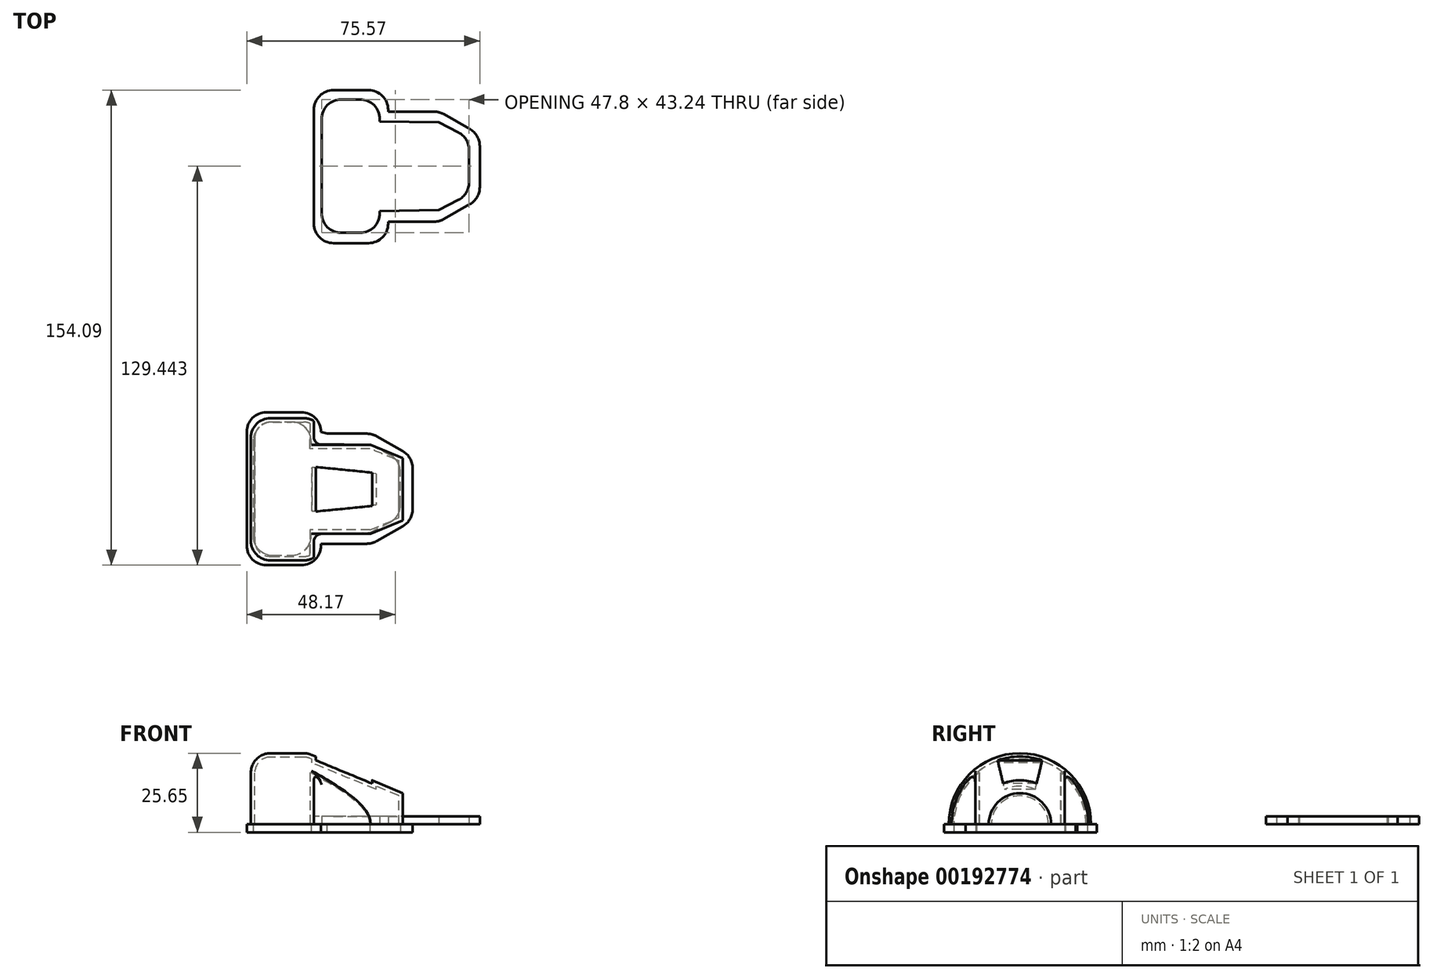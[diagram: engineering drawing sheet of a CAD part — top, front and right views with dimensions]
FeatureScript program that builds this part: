
annotation { "Feature Type Name" : "Feature", "Feature Type Description" : "" }
export const myFeature = defineFeature(function(context is Context, id is Id, definition is map)
    precondition{}
    {
        {
            var Q0;
            Q0=qCreatedBy(makeId("Top.planeOp"),FACE);
            var sketch = newSketch(context, id + "F0", { "sketchPlane" : qUnion([Q0])});
            skLineSegment(sketch, "E0.right", {"start": v(46.79, -59.1) * mm, "end": v(46.79, -37.32) * mm});
            skLineSegment(sketch, "E1", {"start": v(46.79, -37.32) * mm, "end": v(76.56, -49.84) * mm});
            skLineSegment(sketch, "E2", {"start": v(76.56, -49.84) * mm, "end": v(76.56, -59.1) * mm});
            skLineSegment(sketch, "E3", {"start": v(76.56, -59.1) * mm, "end": v(46.79, -59.1) * mm});
            skLineSegment(sketch, "E4.bottom", {"start": v(29.86, -59.1) * mm, "end": v(46.79, -59.1) * mm});
            skLineSegment(sketch, "E4.top", {"start": v(29.86, -37.32) * mm, "end": v(46.79, -37.32) * mm});
            skLineSegment(sketch, "E4.left", {"start": v(29.86, -59.1) * mm, "end": v(29.86, -37.32) * mm});
            skSolve(sketch);
        }
        {
            var Q0;
            Q0=qCreatedBy(makeId("Top.planeOp"),FACE);
            var sketch = newSketch(context, id + "F1", { "sketchPlane" : qUnion([Q0])});
            skLineSegment(sketch, "E5", {"start": v(49.04, 32.89) * mm, "end": v(49.04, 27.09) * mm});
            skLineSegment(sketch, "E6", {"start": v(55.39, 20.74) * mm, "end": v(66.76, 20.74) * mm});
            skLineSegment(sketch, "E7", {"start": v(73.1, 27.09) * mm, "end": v(73.1, 27.7) * mm});
            skLineSegment(sketch, "E8", {"start": v(73.1, 27.7) * mm, "end": v(88, 27.7) * mm});
            skLineSegment(sketch, "E9", {"start": v(-9.46, 33.17) * mm, "end": v(-27.89, 38.87) * mm});
            skLineSegment(sketch, "E10", {"start": v(91.13, 28.53) * mm, "end": v(99.61, 33.36) * mm});
            skLineSegment(sketch, "E11", {"start": v(102.82, 38.88) * mm, "end": v(102.82, 45.55) * mm});
            skLineSegment(sketch, "E12", {"start": v(-32.36, 44.94) * mm, "end": v(-32.36, 45.55) * mm});
            skLineSegment(sketch, "E13.MirrorCS", {"start": v(-32.36, 46.16) * mm, "end": v(-32.36, 45.55) * mm});
            skLineSegment(sketch, "E14.MirrorCS", {"start": v(-9.46, 57.93) * mm, "end": v(-27.89, 52.23) * mm});
            skLineSegment(sketch, "E15.MirrorCS", {"start": v(49.04, 58.2) * mm, "end": v(49.04, 64) * mm});
            skLineSegment(sketch, "E16.MirrorCS", {"start": v(55.39, 70.36) * mm, "end": v(66.76, 70.36) * mm});
            skLineSegment(sketch, "E17.MirrorCS", {"start": v(73.1, 64) * mm, "end": v(73.1, 63.4) * mm});
            skLineSegment(sketch, "E18.MirrorCS", {"start": v(73.1, 63.4) * mm, "end": v(88, 63.4) * mm});
            skLineSegment(sketch, "E19.MirrorCS", {"start": v(91.13, 62.56) * mm, "end": v(99.61, 57.74) * mm});
            skLineSegment(sketch, "E20.MirrorCS", {"start": v(102.82, 52.22) * mm, "end": v(102.82, 45.55) * mm});
            skPoint(sketch, "E21.visualSharp", {"position": v(49.04, 20.74) * mm});
            skArc(sketch, "E21.filletArc", {"start": v(49.04, 27.09) * mm, "mid": v(50.9, 22.6) * mm, "end": v(55.39, 20.74) * mm});
            skPoint(sketch, "E22.visualSharp", {"position": v(73.1, 20.74) * mm});
            skArc(sketch, "E22.filletArc", {"start": v(66.76, 20.74) * mm, "mid": v(71.25, 22.6) * mm, "end": v(73.1, 27.09) * mm});
            skPoint(sketch, "E23.visualSharp", {"position": v(49.04, 70.36) * mm});
            skArc(sketch, "E23.filletArc", {"start": v(55.39, 70.36) * mm, "mid": v(50.9, 68.5) * mm, "end": v(49.04, 64) * mm});
            skPoint(sketch, "E24.visualSharp", {"position": v(73.1, 70.36) * mm});
            skArc(sketch, "E24.filletArc", {"start": v(73.1, 64) * mm, "mid": v(71.25, 68.5) * mm, "end": v(66.76, 70.36) * mm});
            skPoint(sketch, "E25.visualSharp", {"position": v(102.82, 55.91) * mm});
            skArc(sketch, "E25.filletArc", {"start": v(102.82, 52.22) * mm, "mid": v(101.96, 55.41) * mm, "end": v(99.61, 57.74) * mm});
            skPoint(sketch, "E26.visualSharp", {"position": v(102.82, 35.18) * mm});
            skArc(sketch, "E26.filletArc", {"start": v(99.61, 33.36) * mm, "mid": v(101.96, 35.68) * mm, "end": v(102.82, 38.88) * mm});
            skPoint(sketch, "E27.visualSharp", {"position": v(89.67, 63.4) * mm});
            skArc(sketch, "E27.filletArc", {"start": v(91.13, 62.56) * mm, "mid": v(89.62, 63.18) * mm, "end": v(88, 63.4) * mm});
            skPoint(sketch, "E28.visualSharp", {"position": v(89.67, 27.7) * mm});
            skArc(sketch, "E28.filletArc", {"start": v(88, 27.7) * mm, "mid": v(89.62, 27.91) * mm, "end": v(91.13, 28.53) * mm});
            skPoint(sketch, "E29.visualSharp", {"position": v(-8.54, 58.2) * mm});
            skArc(sketch, "E29.filletArc", {"start": v(-7.58, 58.2) * mm, "mid": v(-8.53, 58.14) * mm, "end": v(-9.46, 57.93) * mm});
            skPoint(sketch, "E30.visualSharp", {"position": v(-8.54, 32.89) * mm});
            skArc(sketch, "E30.filletArc", {"start": v(-9.46, 33.17) * mm, "mid": v(-8.53, 32.96) * mm, "end": v(-7.58, 32.89) * mm});
            skPoint(sketch, "E31.visualSharp", {"position": v(-32.36, 40.25) * mm});
            skArc(sketch, "E31.filletArc", {"start": v(-32.36, 44.94) * mm, "mid": v(-31.12, 41.17) * mm, "end": v(-27.89, 38.87) * mm});
            skPoint(sketch, "E32.visualSharp", {"position": v(-32.36, 50.84) * mm});
            skArc(sketch, "E32.filletArc", {"start": v(-27.89, 52.23) * mm, "mid": v(-31.12, 49.93) * mm, "end": v(-32.36, 46.16) * mm});
            skLineSegment(sketch, "E33", {"start": v(49.04, 58.2) * mm, "end": v(49.04, 32.89) * mm});
            skSolve(sketch);
        }
        {
            var Q0;
            Q0=makeQuery(id+"F0.imprint","IMPRINT",FACE,{"disambiguationData":[TD([[makeQuery(id+"F0.imprint","IMPRINT",EDGE,{"derivedFrom":sQuery(id+"F0.wireOp",EDGE,"E4.bottom")}),1.0]])]});
            var Q1;
            Q1=makeQuery(id+"F0.imprint","IMPRINT",FACE,{"disambiguationData":[TD([[makeQuery(id+"F0.imprint","IMPRINT",EDGE,{"derivedFrom":sQuery(id+"F0.wireOp",EDGE,"E1")}),-1.0]])]});
            var Q2;
            Q2=sQuery(id+"F0.wireOp",EDGE,"E4.bottom");
            revolve(context, id + "F2", {"entities" : qUnion([Q0, Q1]), "axis" : qUnion([Q2]), "revolveType" : RevolveType.ONE_DIRECTION, "angle" : 180 * degree});
        }
        {
            var Q0;
            Q0=makeQuery(id+"F2.opRevolve","SWEPT_EDGE",EDGE,{"disambiguationData":[OSD([sQuery(id+"F0.wireOp",EDGE,"E1"),sQuery(id+"F0.wireOp",EDGE,"E4.top"),sQuery(id+"F0.wireOp",EDGE,"E0.right")])]});
            var Q1;
            Q1=makeQuery(id+"F2.opRevolve","SWEPT_EDGE",EDGE,{"disambiguationData":[OSD([sQuery(id+"F0.wireOp",EDGE,"E4.top"),sQuery(id+"F0.wireOp",EDGE,"E4.left")])]});
            fillet(context, id + "F3", {"entities" : qUnion([Q0, Q1]), "radius" : 5.08 * mm, "tangentPropagation" : true, "allowEdgeOverflow" : false});
        }
        {
            var Q0;
            Q0=qCreatedBy(makeId("Top.planeOp"),FACE);
            var sketch = newSketch(context, id + "F4", { "sketchPlane" : qUnion([Q0])});
            skLineSegment(sketch, "E34.0.0", {"start": v(34.94, -37.32) * mm, "end": v(45.76, -37.32) * mm});
            skArc(sketch, "E34.0.1", {"start": v(45.76, -37.32) * mm, "mid": v(46.77, -37.42) * mm, "end": v(47.73, -37.71) * mm});
            skLineSegment(sketch, "E34.0.2", {"start": v(47.73, -37.71) * mm, "end": v(76.56, -49.84) * mm});
            skLineSegment(sketch, "E34.0.3", {"start": v(76.56, -49.84) * mm, "end": v(76.56, -68.37) * mm});
            skLineSegment(sketch, "E34.0.4", {"start": v(76.56, -68.37) * mm, "end": v(47.73, -80.5) * mm});
            skArc(sketch, "E34.0.5", {"start": v(47.73, -80.5) * mm, "mid": v(46.77, -80.8) * mm, "end": v(45.76, -80.9) * mm});
            skLineSegment(sketch, "E34.0.6", {"start": v(45.76, -80.9) * mm, "end": v(34.94, -80.9) * mm});
            skArc(sketch, "E34.0.7", {"start": v(34.94, -80.9) * mm, "mid": v(31.35, -79.4) * mm, "end": v(29.86, -75.82) * mm});
            skLineSegment(sketch, "E34.0.8", {"start": v(29.86, -75.82) * mm, "end": v(29.86, -42.4) * mm});
            skArc(sketch, "E34.0.9", {"start": v(29.86, -42.4) * mm, "mid": v(31.35, -38.8) * mm, "end": v(34.94, -37.32) * mm});
            skLineSegment(sketch, "E35", {"start": v(47.73, -82.32) * mm, "end": v(47.73, -72.3) * mm});
            skLineSegment(sketch, "E36", {"start": v(47.73, -72.3) * mm, "end": v(75.84, -72.3) * mm});
            skLineSegment(sketch, "E37", {"start": v(75.84, -72.3) * mm, "end": v(75.51, -83.4) * mm});
            skLineSegment(sketch, "E38", {"start": v(75.51, -83.4) * mm, "end": v(47.73, -82.32) * mm});
            skLineSegment(sketch, "E39.MirrorCS", {"start": v(47.73, -45.9) * mm, "end": v(75.84, -45.9) * mm});
            skLineSegment(sketch, "E40.MirrorCS", {"start": v(75.51, -34.8) * mm, "end": v(47.73, -35.89) * mm});
            skLineSegment(sketch, "E41.MirrorCS", {"start": v(47.73, -35.89) * mm, "end": v(47.73, -45.9) * mm});
            skLineSegment(sketch, "E42.MirrorCS", {"start": v(75.84, -45.9) * mm, "end": v(75.51, -34.8) * mm});
            skSolve(sketch);
        }
        {
            var Q0;
            {var subQ0=sQuery(id+"F4.wireOp",EDGE,"E35");var subQ3=sQuery(id+"F4.wireOp",EDGE,"E36");var subQ5=makeQuery(id+"F4.imprint","INTERSECT",VERTEX,{"derivedFrom":[subQ0,subQ3]});Q0=makeQuery(id+"F4.imprint","IMPRINT",FACE,{"disambiguationData":[TD([[makeQuery(id+"F4.imprint","IMPRINT",EDGE,{"disambiguationData":[TD([[subQ5,-1.0]])],"derivedFrom":subQ3}),-1.0]])]});}
            var Q1;
            {var subQ0=sQuery(id+"F4.wireOp",EDGE,"E41.MirrorCS");var subQ3=sQuery(id+"F4.wireOp",EDGE,"E39.MirrorCS");var subQ5=makeQuery(id+"F4.imprint","INTERSECT",VERTEX,{"derivedFrom":[subQ3,subQ0]});Q1=makeQuery(id+"F4.imprint","IMPRINT",FACE,{"disambiguationData":[TD([[makeQuery(id+"F4.imprint","IMPRINT",EDGE,{"disambiguationData":[TD([[subQ5,-1.0]])],"derivedFrom":subQ3}),1.0]])]});}
            var Q2;
            {var subQ3=sQuery(id+"F4.wireOp",EDGE,"E40.MirrorCS");Q2=makeQuery(id+"F4.imprint","IMPRINT",FACE,{"disambiguationData":[TD([[makeQuery(id+"F4.imprint","IMPRINT",EDGE,{"derivedFrom":subQ3}),1.0]])]});}
            var Q3;
            {var subQ0=sQuery(id+"F4.wireOp",EDGE,"E37");Q3=makeQuery(id+"F4.imprint","IMPRINT",FACE,{"disambiguationData":[TD([[makeQuery(id+"F4.imprint","IMPRINT",EDGE,{"derivedFrom":subQ0}),-1.0]])]});}
            extrude(context, id + "F5", {"entities" : qUnion([Q0, Q1, Q2, Q3]), "operationType" : NewBodyOperationType.REMOVE, "depth" : 25.4 * mm});
        }
        {
            var Q0;
            Q0=makeQuery(id+"F5.boolean.opBoolean","COPY",FACE,{"derivedFrom":makeQuery(id+"F5.opExtrude","SWEPT_FACE",FACE,{"disambiguationData":[OSD([sQuery(id+"F4.wireOp",EDGE,"E36")])]})});
            var sketch = newSketch(context, id + "F6", { "sketchPlane" : qUnion([Q0])});
            skLineSegment(sketch, "E43", {"start": v(48.34, 28.45) * mm, "end": v(48.34, 19.91) * mm});
            skLineSegment(sketch, "E44", {"start": v(48.34, 19.91) * mm, "end": v(69.19, 11.32) * mm});
            skLineSegment(sketch, "E45", {"start": v(69.19, 11.32) * mm, "end": v(69.19, 27.77) * mm});
            skLineSegment(sketch, "E46", {"start": v(69.19, 27.77) * mm, "end": v(48.34, 28.45) * mm});
            skSolve(sketch);
        }
        {
            var Q0;
            Q0=makeQuery(id+"F6.imprint","IMPRINT",FACE,{"disambiguationData":[TD([[makeQuery(id+"F6.imprint","IMPRINT",EDGE,{"derivedFrom":sQuery(id+"F6.wireOp",EDGE,"E43")}),1.0]])]});
            extrude(context, id + "F7", {"entities" : qUnion([Q0]), "operationType" : NewBodyOperationType.REMOVE, "oppositeDirection" : true, "depth" : 50.8 * mm});
        }
        {
            var Q0;
            Q0=makeQuery(id+"F2.opRevolve","CAP_FACE",FACE,{"disambiguationData":[OSD([sQuery(id+"F0.wireOp",EDGE,"E1"),sQuery(id+"F0.wireOp",EDGE,"E2"),sQuery(id+"F0.wireOp",EDGE,"E3"),sQuery(id+"F0.wireOp",EDGE,"E4.bottom"),sQuery(id+"F0.wireOp",EDGE,"E4.top"),sQuery(id+"F0.wireOp",EDGE,"E4.left")])],"isStart":false});
            shell(context, id + "F8", {"entities" : qUnion([Q0]), "thickness" : 1.27 * mm, "oppositeDirection" : true});
        }
        {
            var Q0;
            Q0=makeQuery(id+"F1.imprint","IMPRINT",FACE,{"disambiguationData":[TD([[makeQuery(id+"F1.imprint","IMPRINT",EDGE,{"derivedFrom":sQuery(id+"F1.wireOp",EDGE,"E5")}),1.0]])]});
            extrude(context, id + "F9", {"entities" : qUnion([Q0]), "depth" : 2.54 * mm});
        }
        {
            var Q0;
            Q0=makeQuery(id+"F1.imprint","IMPRINT",FACE,{"disambiguationData":[TD([[makeQuery(id+"F1.imprint","IMPRINT",EDGE,{"derivedFrom":sQuery(id+"F1.wireOp",EDGE,"E5")}),1.0]])]});
            var sketch = newSketch(context, id + "F10", { "sketchPlane" : qUnion([Q0])});
            skLineSegment(sketch, "E47", {"start": v(103.17, 45.71) * mm, "end": v(28.73, 45.71) * mm, "construction": true});
            skLineSegment(sketch, "E48", {"start": v(51.52, 45.71) * mm, "end": v(51.52, 30.44) * mm});
            skLineSegment(sketch, "E49", {"start": v(57.87, 24.1) * mm, "end": v(64.04, 24.1) * mm});
            skLineSegment(sketch, "E50", {"start": v(70.39, 30.44) * mm, "end": v(70.39, 31.17) * mm});
            skLineSegment(sketch, "E51", {"start": v(70.39, 31.17) * mm, "end": v(89.48, 31.46) * mm});
            skLineSegment(sketch, "E52", {"start": v(89.48, 31.46) * mm, "end": v(95.88, 34.76) * mm});
            skLineSegment(sketch, "E53", {"start": v(112.09, -4.68) * mm, "end": v(112.09, -10.48) * mm});
            skLineSegment(sketch, "E54", {"start": v(118.44, -16.83) * mm, "end": v(129.8, -16.83) * mm});
            skLineSegment(sketch, "E55", {"start": v(136.15, -10.48) * mm, "end": v(136.15, -9.86) * mm});
            skLineSegment(sketch, "E56", {"start": v(136.15, -9.86) * mm, "end": v(151.04, -9.86) * mm});
            skLineSegment(sketch, "E57", {"start": v(154.18, -9.03) * mm, "end": v(162.66, -4.2) * mm});
            skLineSegment(sketch, "E58", {"start": v(165.87, 1.31) * mm, "end": v(165.87, 7.99) * mm});
            skLineSegment(sketch, "E59.MirrorCS", {"start": v(112.09, 20.65) * mm, "end": v(112.09, 26.45) * mm});
            skLineSegment(sketch, "E60.MirrorCS", {"start": v(118.44, 32.8) * mm, "end": v(129.8, 32.8) * mm});
            skLineSegment(sketch, "E61.MirrorCS", {"start": v(136.15, 26.45) * mm, "end": v(136.15, 25.83) * mm});
            skLineSegment(sketch, "E62.MirrorCS", {"start": v(136.15, 25.83) * mm, "end": v(151.04, 25.83) * mm});
            skLineSegment(sketch, "E63.MirrorCS", {"start": v(154.18, 25) * mm, "end": v(162.66, 20.18) * mm});
            skLineSegment(sketch, "E64.MirrorCS", {"start": v(165.87, 14.66) * mm, "end": v(165.87, 7.99) * mm});
            skPoint(sketch, "E65.visualSharp", {"position": v(112.09, -16.83) * mm});
            skArc(sketch, "E65.filletArc", {"start": v(112.09, -10.48) * mm, "mid": v(113.95, -14.97) * mm, "end": v(118.44, -16.83) * mm});
            skPoint(sketch, "E66.visualSharp", {"position": v(136.15, -16.83) * mm});
            skArc(sketch, "E66.filletArc", {"start": v(129.8, -16.83) * mm, "mid": v(134.3, -14.97) * mm, "end": v(136.15, -10.48) * mm});
            skPoint(sketch, "E67.visualSharp", {"position": v(112.09, 32.8) * mm});
            skArc(sketch, "E67.filletArc", {"start": v(118.44, 32.8) * mm, "mid": v(113.95, 30.94) * mm, "end": v(112.09, 26.45) * mm});
            skPoint(sketch, "E68.visualSharp", {"position": v(136.15, 32.8) * mm});
            skArc(sketch, "E68.filletArc", {"start": v(136.15, 26.45) * mm, "mid": v(134.3, 30.94) * mm, "end": v(129.8, 32.8) * mm});
            skPoint(sketch, "E69.visualSharp", {"position": v(165.87, 18.35) * mm});
            skArc(sketch, "E69.filletArc", {"start": v(165.87, 14.66) * mm, "mid": v(165, 17.85) * mm, "end": v(162.66, 20.18) * mm});
            skPoint(sketch, "E70.visualSharp", {"position": v(165.87, -2.38) * mm});
            skArc(sketch, "E70.filletArc", {"start": v(162.66, -4.2) * mm, "mid": v(165, -1.88) * mm, "end": v(165.87, 1.31) * mm});
            skPoint(sketch, "E71.visualSharp", {"position": v(152.72, 25.83) * mm});
            skArc(sketch, "E71.filletArc", {"start": v(154.18, 25) * mm, "mid": v(152.66, 25.62) * mm, "end": v(151.04, 25.83) * mm});
            skPoint(sketch, "E72.visualSharp", {"position": v(152.72, -9.86) * mm});
            skArc(sketch, "E72.filletArc", {"start": v(151.04, -9.86) * mm, "mid": v(152.66, -9.65) * mm, "end": v(154.18, -9.03) * mm});
            skLineSegment(sketch, "E73", {"start": v(112.09, 20.65) * mm, "end": v(112.09, -4.68) * mm});
            skLineSegment(sketch, "E74", {"start": v(99.32, 45.71) * mm, "end": v(99.32, 40.4) * mm});
            skLineSegment(sketch, "E75.MirrorCS", {"start": v(99.32, 45.71) * mm, "end": v(99.32, 51.02) * mm});
            skLineSegment(sketch, "E76.MirrorCS", {"start": v(89.48, 59.97) * mm, "end": v(95.88, 56.67) * mm});
            skLineSegment(sketch, "E77.MirrorCS", {"start": v(70.39, 60.98) * mm, "end": v(70.39, 60.26) * mm});
            skLineSegment(sketch, "E78.MirrorCS", {"start": v(70.39, 60.26) * mm, "end": v(89.48, 59.97) * mm});
            skLineSegment(sketch, "E79.MirrorCS", {"start": v(57.87, 67.33) * mm, "end": v(64.04, 67.33) * mm});
            skLineSegment(sketch, "E80.MirrorCS", {"start": v(51.52, 45.71) * mm, "end": v(51.52, 60.98) * mm});
            skPoint(sketch, "E81.visualSharp", {"position": v(70.39, 24.1) * mm});
            skArc(sketch, "E81.filletArc", {"start": v(64.04, 24.1) * mm, "mid": v(68.53, 25.95) * mm, "end": v(70.39, 30.44) * mm});
            skPoint(sketch, "E82.visualSharp", {"position": v(70.39, 67.33) * mm});
            skArc(sketch, "E82.filletArc", {"start": v(70.39, 60.98) * mm, "mid": v(68.53, 65.47) * mm, "end": v(64.04, 67.33) * mm});
            skPoint(sketch, "E83.visualSharp", {"position": v(51.52, 24.1) * mm});
            skArc(sketch, "E83.filletArc", {"start": v(51.52, 30.44) * mm, "mid": v(53.38, 25.95) * mm, "end": v(57.87, 24.1) * mm});
            skPoint(sketch, "E84.newPointB", {"position": v(51.52, 67.33) * mm});
            skArc(sketch, "E84.filletArc", {"start": v(57.87, 67.33) * mm, "mid": v(53.38, 65.47) * mm, "end": v(51.52, 60.98) * mm});
            skPoint(sketch, "E85.visualSharp", {"position": v(99.32, 36.54) * mm});
            skArc(sketch, "E85.filletArc", {"start": v(95.88, 34.76) * mm, "mid": v(98.4, 37.1) * mm, "end": v(99.32, 40.4) * mm});
            skPoint(sketch, "E86.visualSharp", {"position": v(99.32, 54.9) * mm});
            skArc(sketch, "E86.filletArc", {"start": v(99.32, 51.02) * mm, "mid": v(98.4, 54.33) * mm, "end": v(95.88, 56.67) * mm});
            skLineSegment(sketch, "E87", {"start": v(27.25, -72.13) * mm, "end": v(27.25, -77.38) * mm});
            skLineSegment(sketch, "E88", {"start": v(33.6, -83.73) * mm, "end": v(44.97, -83.73) * mm});
            skLineSegment(sketch, "E89", {"start": v(51.32, -77.38) * mm, "end": v(51.32, -76.77) * mm});
            skLineSegment(sketch, "E90", {"start": v(51.32, -76.77) * mm, "end": v(66.2, -76.77) * mm});
            skLineSegment(sketch, "E91", {"start": v(69.34, -75.94) * mm, "end": v(77.82, -71.11) * mm});
            skLineSegment(sketch, "E92", {"start": v(81.03, -65.6) * mm, "end": v(81.03, -59.47) * mm});
            skLineSegment(sketch, "E93.MirrorCS", {"start": v(27.25, -46.8) * mm, "end": v(27.25, -40.46) * mm});
            skLineSegment(sketch, "E94.MirrorCS", {"start": v(33.6, -34.1) * mm, "end": v(44.97, -34.1) * mm});
            skLineSegment(sketch, "E95.MirrorCS", {"start": v(51.32, -40.46) * mm, "end": v(51.32, -41.62) * mm});
            skLineSegment(sketch, "E96.MirrorCS", {"start": v(53.34, -41.07) * mm, "end": v(66.2, -41.07) * mm});
            skLineSegment(sketch, "E97.MirrorCS", {"start": v(69.34, -41.9) * mm, "end": v(77.82, -46.73) * mm});
            skLineSegment(sketch, "E98.MirrorCS", {"start": v(81.03, -52.25) * mm, "end": v(81.03, -59.47) * mm});
            skArc(sketch, "E99.filletArc", {"start": v(27.25, -77.38) * mm, "mid": v(29.1, -81.87) * mm, "end": v(33.6, -83.73) * mm});
            skArc(sketch, "E100.filletArc", {"start": v(44.97, -83.73) * mm, "mid": v(49.46, -81.87) * mm, "end": v(51.32, -77.38) * mm});
            skArc(sketch, "E101.filletArc", {"start": v(33.6, -34.1) * mm, "mid": v(29.1, -35.97) * mm, "end": v(27.25, -40.46) * mm});
            skArc(sketch, "E102.filletArc", {"start": v(51.32, -40.46) * mm, "mid": v(49.46, -35.97) * mm, "end": v(44.97, -34.1) * mm});
            skArc(sketch, "E103.filletArc", {"start": v(81.03, -52.25) * mm, "mid": v(80.17, -49.06) * mm, "end": v(77.82, -46.73) * mm});
            skArc(sketch, "E104.filletArc", {"start": v(77.82, -71.11) * mm, "mid": v(80.17, -68.79) * mm, "end": v(81.03, -65.6) * mm});
            skArc(sketch, "E105.filletArc", {"start": v(69.34, -41.9) * mm, "mid": v(67.82, -41.29) * mm, "end": v(66.2, -41.07) * mm});
            skArc(sketch, "E106.filletArc", {"start": v(66.2, -76.77) * mm, "mid": v(67.82, -76.56) * mm, "end": v(69.34, -75.94) * mm});
            skLineSegment(sketch, "E107", {"start": v(27.25, -46.8) * mm, "end": v(27.25, -72.13) * mm});
            skLineSegment(sketch, "E108", {"start": v(53.34, -41.07) * mm, "end": v(51.32, -40.46) * mm});
            skSolve(sketch);
        }
        {
            var Q0;
            Q0=makeQuery(id+"F10.imprint","IMPRINT",FACE,{"disambiguationData":[TD([[makeQuery(id+"F10.imprint","IMPRINT",EDGE,{"derivedFrom":sQuery(id+"F10.wireOp",EDGE,"E48")}),1.0]])]});
            extrude(context, id + "F11", {"entities" : qUnion([Q0]), "operationType" : NewBodyOperationType.REMOVE, "depth" : 25.4 * mm});
        }
        {
            var Q0;
            Q0=makeQuery(id+"F5.boolean.opBoolean","COPY",EDGE,{"derivedFrom":makeQuery(id+"F5.opExtrude","SWEPT_EDGE",EDGE,{"disambiguationData":[OSD([sQuery(id+"F4.wireOp",EDGE,"E35"),sQuery(id+"F4.wireOp",EDGE,"E36")])]})});
            var Q1;
            Q1=makeQuery(id+"F5.boolean.opBoolean","COPY",EDGE,{"derivedFrom":makeQuery(id+"F5.opExtrude","SWEPT_EDGE",EDGE,{"disambiguationData":[OSD([sQuery(id+"F4.wireOp",EDGE,"E39.MirrorCS"),sQuery(id+"F4.wireOp",EDGE,"E41.MirrorCS")])]})});
            fillet(context, id + "F12", {"entities" : qUnion([Q0, Q1]), "radius" : 2.54 * mm, "tangentPropagation" : true, "allowEdgeOverflow" : false});
        }
        {
            var Q0;
            Q0=makeQuery(id+"F10.imprint","IMPRINT",FACE,{"disambiguationData":[TD([[makeQuery(id+"F10.imprint","IMPRINT",EDGE,{"derivedFrom":sQuery(id+"F10.wireOp",EDGE,"E87")}),1.0]])]});
            extrude(context, id + "F13", {"entities" : qUnion([Q0]), "operationType" : NewBodyOperationType.ADD, "oppositeDirection" : true, "depth" : 2.59 * mm});
        }
        {
            var Q0;
            Q0=makeQuery(id+"F13.opExtrude","CAP_FACE",FACE,{"disambiguationData":[OSD([sQuery(id+"F10.wireOp",EDGE,"E87"),sQuery(id+"F10.wireOp",EDGE,"E88"),sQuery(id+"F10.wireOp",EDGE,"E89"),sQuery(id+"F10.wireOp",EDGE,"E90"),sQuery(id+"F10.wireOp",EDGE,"E91"),sQuery(id+"F10.wireOp",EDGE,"E92"),sQuery(id+"F10.wireOp",EDGE,"E93.MirrorCS"),sQuery(id+"F10.wireOp",EDGE,"E94.MirrorCS"),sQuery(id+"F10.wireOp",EDGE,"E96.MirrorCS"),sQuery(id+"F10.wireOp",EDGE,"E97.MirrorCS"),sQuery(id+"F10.wireOp",EDGE,"E98.MirrorCS"),sQuery(id+"F10.wireOp",EDGE,"E99.filletArc"),sQuery(id+"F10.wireOp",EDGE,"E100.filletArc"),sQuery(id+"F10.wireOp",EDGE,"E104.filletArc"),sQuery(id+"F10.wireOp",EDGE,"E106.filletArc"),sQuery(id+"F10.wireOp",EDGE,"E101.filletArc"),sQuery(id+"F10.wireOp",EDGE,"E102.filletArc"),sQuery(id+"F10.wireOp",EDGE,"E103.filletArc"),sQuery(id+"F10.wireOp",EDGE,"E105.filletArc"),sQuery(id+"F10.wireOp",EDGE,"E107"),sQuery(id+"F10.wireOp",EDGE,"E108")])],"isStart":false});
            var sketch = newSketch(context, id + "F14", { "sketchPlane" : qUnion([Q0])});
            skLineSegment(sketch, "E109", {"start": v(29.28, 59.65) * mm, "end": v(29.28, 43.62) * mm});
            skLineSegment(sketch, "E110", {"start": v(35.63, 37.27) * mm, "end": v(41.8, 37.27) * mm});
            skLineSegment(sketch, "E111", {"start": v(48.15, 43.62) * mm, "end": v(48.15, 44.35) * mm});
            skLineSegment(sketch, "E112", {"start": v(48.15, 44.35) * mm, "end": v(67.25, 44.64) * mm});
            skLineSegment(sketch, "E113", {"start": v(67.25, 44.64) * mm, "end": v(73.65, 47.94) * mm});
            skLineSegment(sketch, "E114", {"start": v(77.09, 59.65) * mm, "end": v(77.09, 53.58) * mm});
            skLineSegment(sketch, "E115.MirrorCS", {"start": v(77.09, 59.65) * mm, "end": v(77.09, 64.2) * mm});
            skLineSegment(sketch, "E116.MirrorCS", {"start": v(65.26, 74.18) * mm, "end": v(73.65, 69.85) * mm});
            skLineSegment(sketch, "E117.MirrorCS", {"start": v(48.15, 74.2) * mm, "end": v(48.15, 74.16) * mm});
            skLineSegment(sketch, "E118.MirrorCS", {"start": v(48.15, 73.44) * mm, "end": v(68.65, 73.13) * mm});
            skLineSegment(sketch, "E119.MirrorCS", {"start": v(35.63, 80.51) * mm, "end": v(41.8, 80.51) * mm});
            skLineSegment(sketch, "E120.MirrorCS", {"start": v(29.28, 59.65) * mm, "end": v(29.28, 74.16) * mm});
            skArc(sketch, "E121.filletArc", {"start": v(41.8, 37.27) * mm, "mid": v(46.3, 39.13) * mm, "end": v(48.15, 43.62) * mm});
            skArc(sketch, "E122.filletArc", {"start": v(48.15, 74.16) * mm, "mid": v(46.3, 78.65) * mm, "end": v(41.8, 80.51) * mm});
            skArc(sketch, "E123.filletArc", {"start": v(29.28, 43.62) * mm, "mid": v(31.14, 39.13) * mm, "end": v(35.63, 37.27) * mm});
            skArc(sketch, "E124.filletArc", {"start": v(35.63, 80.51) * mm, "mid": v(31.14, 78.65) * mm, "end": v(29.28, 74.16) * mm});
            skPoint(sketch, "E125.visualSharp", {"position": v(77.09, 49.72) * mm});
            skArc(sketch, "E125.filletArc", {"start": v(73.65, 47.94) * mm, "mid": v(76.16, 50.28) * mm, "end": v(77.09, 53.58) * mm});
            skArc(sketch, "E126.filletArc", {"start": v(77.09, 64.2) * mm, "mid": v(76.16, 67.5) * mm, "end": v(73.65, 69.85) * mm});
            skLineSegment(sketch, "E127", {"start": v(48.15, 74.2) * mm, "end": v(48.15, 73.44) * mm});
            skSolve(sketch);
        }
        {
            var Q0;
            Q0=makeQuery(id+"F14.imprint","IMPRINT",FACE,{"disambiguationData":[TD([[makeQuery(id+"F14.imprint","IMPRINT",EDGE,{"derivedFrom":sQuery(id+"F14.wireOp",EDGE,"E109")}),1.0]])]});
            extrude(context, id + "F15", {"entities" : qUnion([Q0]), "operationType" : NewBodyOperationType.REMOVE, "oppositeDirection" : true, "depth" : 2.8 * mm});
        }
    });
